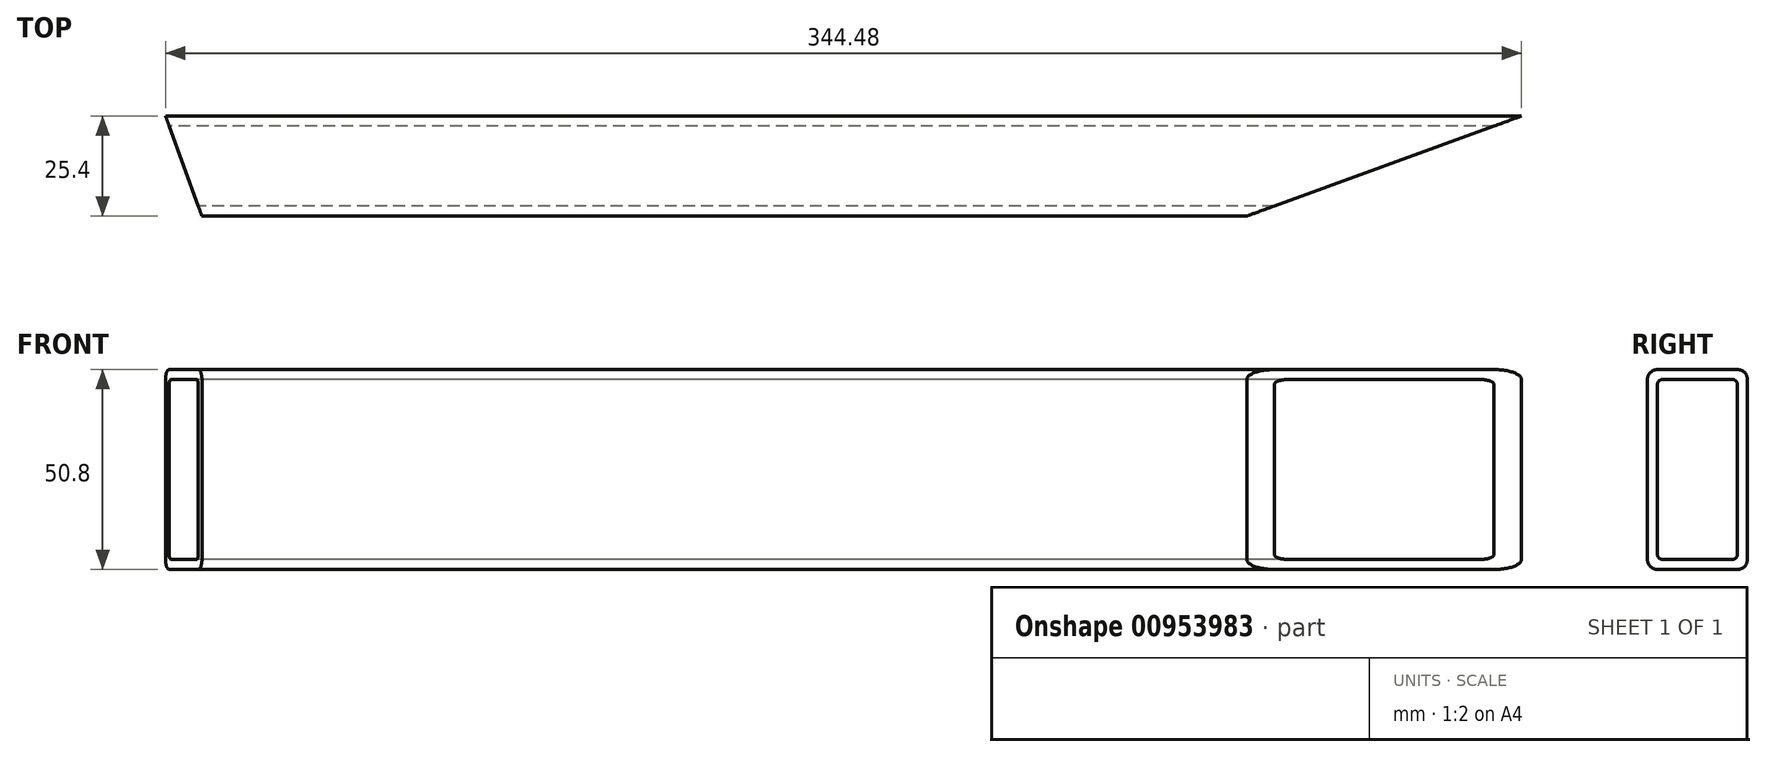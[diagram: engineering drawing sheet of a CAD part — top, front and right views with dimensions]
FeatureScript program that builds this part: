
annotation { "Feature Type Name" : "Feature", "Feature Type Description" : "" }
export const myFeature = defineFeature(function(context is Context, id is Id, definition is map)
    precondition{}
    {
        {
            var Q0;
            Q0=qCreatedBy(makeId("Front.planeOp"),FACE);
            var sketch = newSketch(context, id + "F0", { "sketchPlane" : qUnion([Q0])});
            skLineSegment(sketch, "E0.bottom", {"start": v(172.24, -25.4) * mm, "end": v(-172.24, -25.4) * mm});
            skLineSegment(sketch, "E0.top", {"start": v(172.24, 25.4) * mm, "end": v(-172.24, 25.4) * mm});
            skLineSegment(sketch, "E0.left", {"start": v(172.24, -25.4) * mm, "end": v(172.24, 25.4) * mm});
            skLineSegment(sketch, "E0.right", {"start": v(-172.24, -25.4) * mm, "end": v(-172.24, 25.4) * mm});
            skPoint(sketch, "E0.middle", {"position": v(0, 0) * mm});
            skSolve(sketch);
        }
        {
            var Q0;
            Q0=makeQuery(id+"F0.imprint","IMPRINT",FACE,{"disambiguationData":[TD([[makeQuery(id+"F0.imprint","IMPRINT",EDGE,{"derivedFrom":sQuery(id+"F0.wireOp",EDGE,"E0.bottom")}),-1.0]])]});
            extrude(context, id + "F1", {"entities" : qUnion([Q0]), "endBound" : BoundingType.SYMMETRIC, "depth" : 25.4 * mm, "offsetDistance" : 25.4 * mm});
        }
        {
            var Q0;
            Q0=makeQuery(id+"F1.opExtrude","SWEPT_FACE",FACE,{"disambiguationData":[OSD([sQuery(id+"F0.wireOp",EDGE,"E0.right")])]});
            var Q1;
            Q1=makeQuery(id+"F1.opExtrude","SWEPT_FACE",FACE,{"disambiguationData":[OSD([sQuery(id+"F0.wireOp",EDGE,"E0.left")])]});
            shell(context, id + "F2", {"entities" : qUnion([Q0, Q1]), "thickness" : 2.54 * mm});
        }
        {
            var Q0;
            Q0=makeQuery(id+"F1.opExtrude","SWEPT_FACE",FACE,{"disambiguationData":[OSD([sQuery(id+"F0.wireOp",EDGE,"E0.top")])]});
            var sketch = newSketch(context, id + "F3", { "sketchPlane" : qUnion([Q0])});
            skLineSegment(sketch, "E1", {"start": v(-172.24, 12.7) * mm, "end": v(-172.24, -12.7) * mm});
            skLineSegment(sketch, "E2", {"start": v(-163, -12.7) * mm, "end": v(-172.24, 12.7) * mm});
            skLineSegment(sketch, "E3", {"start": v(-163, -12.7) * mm, "end": v(-172.24, -12.7) * mm});
            skSolve(sketch);
        }
        {
            var Q0;
            Q0=makeQuery(id+"F3.imprint","IMPRINT",FACE,{"disambiguationData":[TD([[makeQuery(id+"F3.imprint","IMPRINT",EDGE,{"derivedFrom":sQuery(id+"F3.wireOp",EDGE,"qf3VPhwr-v0nz-ToZz-LBk7-LaFnvqgaNhO0")}),1.0]])]});
            var Q1;
            Q1=makeQuery(id+"F3.imprint","IMPRINT",FACE,{"disambiguationData":[TD([[makeQuery(id+"F3.imprint","IMPRINT",EDGE,{"derivedFrom":sQuery(id+"F3.wireOp",EDGE,"E1")}),-1.0]])]});
            extrude(context, id + "F4", {"entities" : qUnion([Q0, Q1]), "operationType" : NewBodyOperationType.REMOVE, "endBound" : BoundingType.THROUGH_ALL, "oppositeDirection" : true, "depth" : 25.4 * mm, "offsetDistance" : 25.4 * mm});
        }
        {
            var Q0;
            Q0=makeQuery(id+"F1.opExtrude","SWEPT_FACE",FACE,{"disambiguationData":[OSD([sQuery(id+"F0.wireOp",EDGE,"E0.top")])]});
            var sketch = newSketch(context, id + "F5", { "sketchPlane" : qUnion([Q0])});
            skLineSegment(sketch, "E4", {"start": v(172.24, 12.7) * mm, "end": v(172.24, -12.7) * mm});
            skLineSegment(sketch, "E5", {"start": v(172.24, 12.7) * mm, "end": v(102.46, -12.7) * mm});
            skLineSegment(sketch, "E6", {"start": v(102.46, -12.7) * mm, "end": v(172.24, -12.7) * mm});
            skSolve(sketch);
        }
        {
            var Q0;
            Q0=makeQuery(id+"F5.imprint","IMPRINT",FACE,{"disambiguationData":[TD([[makeQuery(id+"F5.imprint","IMPRINT",EDGE,{"derivedFrom":sQuery(id+"F5.wireOp",EDGE,"E4")}),1.0]])]});
            extrude(context, id + "F6", {"entities" : qUnion([Q0]), "operationType" : NewBodyOperationType.REMOVE, "endBound" : BoundingType.THROUGH_ALL, "oppositeDirection" : true, "depth" : 25.4 * mm, "offsetDistance" : 25.4 * mm});
        }
        {
            var Q0;
            Q0=makeQuery(id+"F1.opExtrude","CAP_EDGE",EDGE,{"disambiguationData":[OSD([sQuery(id+"F0.wireOp",EDGE,"E0.top")])],"isStart":false});
            var Q1;
            Q1=makeQuery(id+"F1.opExtrude","CAP_EDGE",EDGE,{"disambiguationData":[OSD([sQuery(id+"F0.wireOp",EDGE,"E0.top")])],"isStart":true});
            var Q2;
            Q2=makeQuery(id+"F1.opExtrude","CAP_EDGE",EDGE,{"disambiguationData":[OSD([sQuery(id+"F0.wireOp",EDGE,"E0.bottom")])],"isStart":true});
            var Q3;
            Q3=makeQuery(id+"F1.opExtrude","CAP_EDGE",EDGE,{"disambiguationData":[OSD([sQuery(id+"F0.wireOp",EDGE,"E0.bottom")])],"isStart":false});
            fillet(context, id + "F7", {"entities" : qUnion([Q0, Q1, Q2, Q3]), "radius" : 2.54 * mm, "tangentPropagation" : true, "allowEdgeOverflow" : false});
        }
        {
            var Q0;
            {var subQ0=sQuery(id+"F0.wireOp",EDGE,"E0.bottom");Q0=makeQuery(id+"F2.opShell","OFFSET_EDGE",EDGE,{"disambiguationData":[OSD([subQ0]),TDD([makeQuery(id+"F1.opExtrude","CAP_EDGE",EDGE,{"disambiguationData":[OSD([subQ0])],"isStart":false})])]});}
            var Q1;
            {var subQ0=sQuery(id+"F0.wireOp",EDGE,"E0.top");Q1=makeQuery(id+"F2.opShell","OFFSET_EDGE",EDGE,{"disambiguationData":[OSD([subQ0]),TDD([makeQuery(id+"F1.opExtrude","CAP_EDGE",EDGE,{"disambiguationData":[OSD([subQ0])],"isStart":false})])]});}
            var Q2;
            {var subQ0=sQuery(id+"F0.wireOp",EDGE,"E0.top");Q2=makeQuery(id+"F2.opShell","OFFSET_EDGE",EDGE,{"disambiguationData":[OSD([subQ0]),TDD([makeQuery(id+"F1.opExtrude","CAP_EDGE",EDGE,{"disambiguationData":[OSD([subQ0])],"isStart":true})])]});}
            var Q3;
            {var subQ0=sQuery(id+"F0.wireOp",EDGE,"E0.bottom");Q3=makeQuery(id+"F2.opShell","OFFSET_EDGE",EDGE,{"disambiguationData":[OSD([subQ0]),TDD([makeQuery(id+"F1.opExtrude","CAP_EDGE",EDGE,{"disambiguationData":[OSD([subQ0])],"isStart":true})])]});}
            fillet(context, id + "F8", {"entities" : qUnion([Q0, Q1, Q2, Q3]), "radius" : 1.27 * mm, "tangentPropagation" : true, "allowEdgeOverflow" : false});
        }
    });
